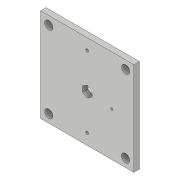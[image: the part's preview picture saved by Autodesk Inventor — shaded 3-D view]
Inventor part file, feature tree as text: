
AUTODESK INVENTOR PART (.ipt)
format: ipt  version: 2019 (Build 230136000, 136)  size: 130,048 bytes
history: native  units: mm
features: extrude x5, sketch x5
ambient origin geometry x8: Origin, YZ Plane, XZ Plane, XY Plane, X Axis, Y Axis, Z Axis, Center Point
bodies: Solid1 (feature_tree)
feature tree (10):
  extrude  "Extrusion1"  Depth=170.0mm
  extrude  "Extrusion2"  Depth=10.0mm
  extrude  "Extrusion3"  Depth=155.0mm
  extrude  "Extrusion4"  Depth=140.0mm
  extrude  "Extrusion5"  Depth=10.0mm
  sketch  "Sketch1"  dims[d0=170.0mm d1=170.0mm]
  sketch  "Sketch2"  dims[d2=10.0mm d3=0.0mm d4=15.0mm]
  sketch  "Sketch3"  dims[d5=15.0mm d6=155.0mm]
  sketch  "Sketch4"  dims[d7=140.0mm d8=140.0mm]
  sketch  "Sketch5"  dims[d9=140.0mm d10=15.0mm d11=15.0mm d12=15.0mm d13=15.0mm d14=10.0mm d15=0.0mm d16=85.0mm d17=85.0mm d18=10.0mm d19=10.0mm d20=0.0mm d21=85.0mm d22=20.0mm d23=130.0mm d24=5.0mm d25=5.0mm d26=10.0mm d27=0.0mm d28=80.0mm d29=40.0mm d30=4.0mm d31=10.0mm d32=0.0mm]
